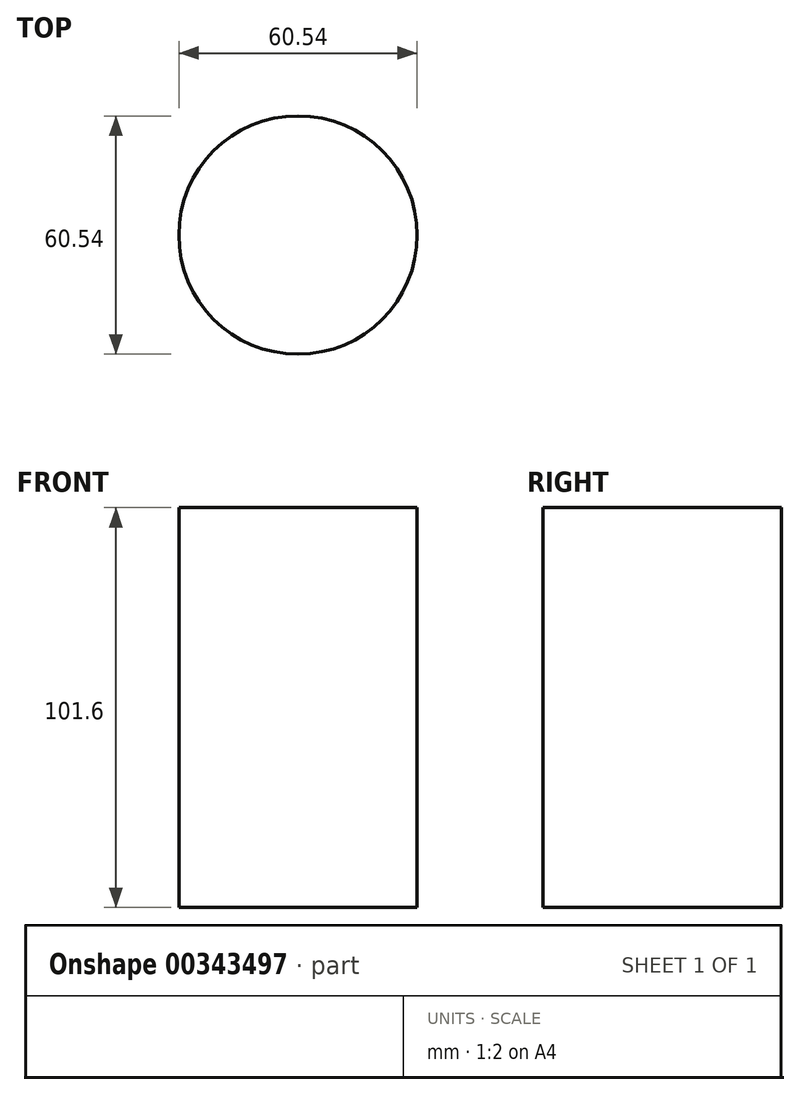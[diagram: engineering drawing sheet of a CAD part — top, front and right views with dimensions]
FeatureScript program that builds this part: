
annotation { "Feature Type Name" : "Feature", "Feature Type Description" : "" }
export const myFeature = defineFeature(function(context is Context, id is Id, definition is map)
    precondition{}
    {
        {
            var Q0;
            Q0=qCreatedBy(makeId("Top.planeOp"),FACE);
            var sketch = newSketch(context, id + "F0", { "sketchPlane" : qUnion([Q0])});
            skCircle(sketch, "E0", {"center": v(0, 0) * mm, "radius": 30.27 * mm});
            skSolve(sketch);
        }
        {
            var Q0;
            Q0=makeQuery(id+"F0.imprint","IMPRINT",FACE,{"disambiguationData":[TD([[makeQuery(id+"F0.imprint","IMPRINT",EDGE,{"derivedFrom":sQuery(id+"F0.wireOp",EDGE,"E0")}),1.0]])]});
            extrude(context, id + "F1", {"entities" : qUnion([Q0]), "depth" : 101.6 * mm});
        }
    });
